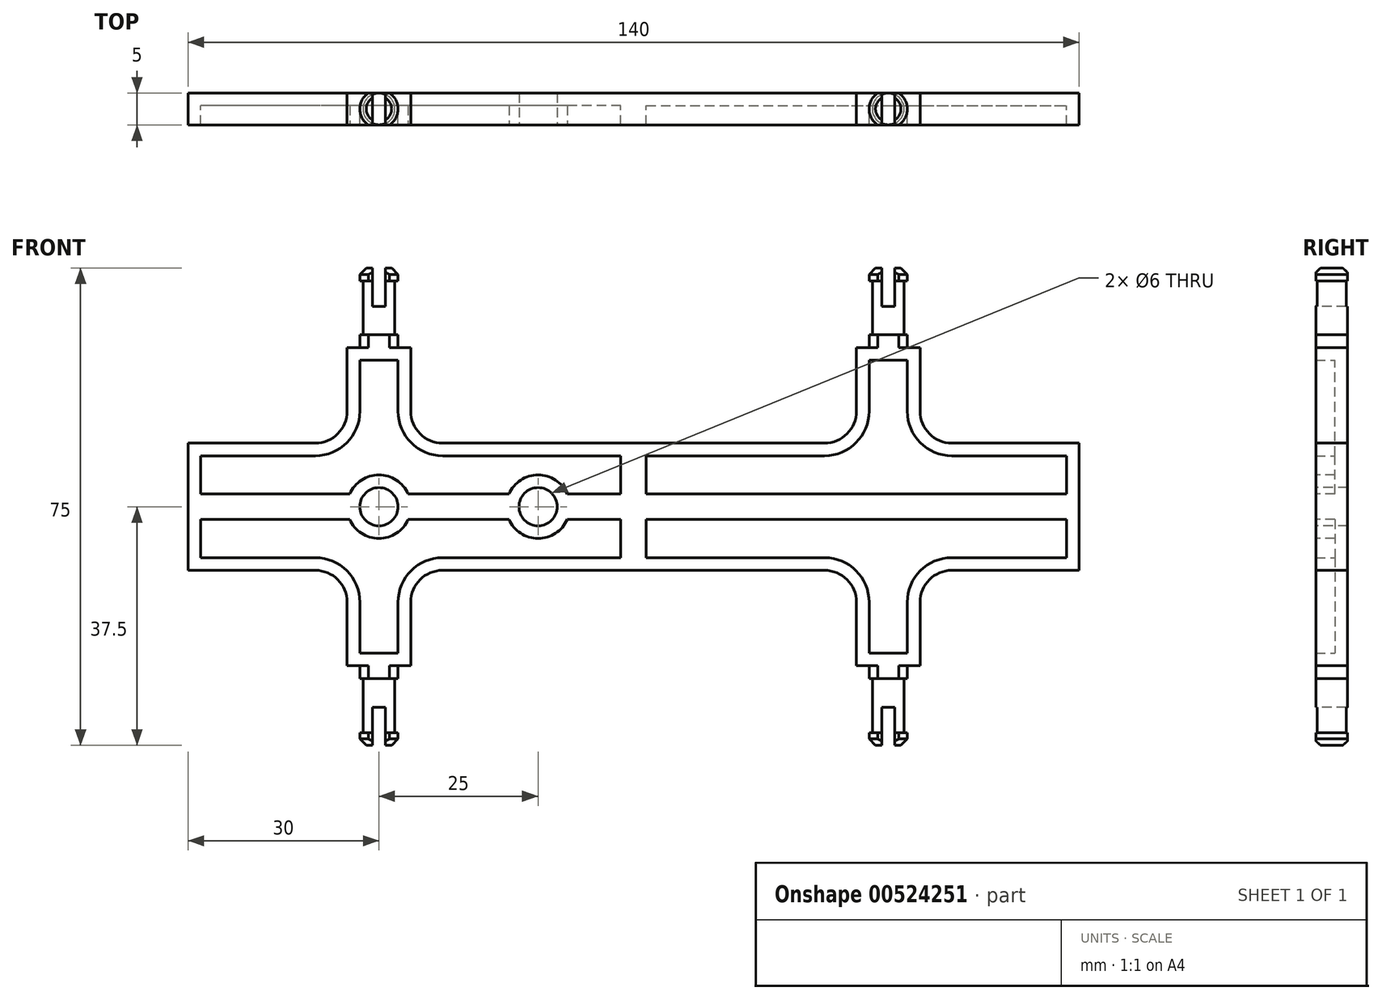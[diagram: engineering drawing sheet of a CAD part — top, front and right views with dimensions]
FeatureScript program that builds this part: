
annotation { "Feature Type Name" : "Feature", "Feature Type Description" : "" }
export const myFeature = defineFeature(function(context is Context, id is Id, definition is map)
    precondition{}
    {
        {
            var Q0;
            Q0=qCreatedBy(makeId("Front.planeOp"),FACE);
            var sketch = newSketch(context, id + "F0", { "sketchPlane" : qUnion([Q0])});
            skLineSegment(sketch, "E0.bottom", {"start": v(0, 0) * mm, "end": v(70, 0) * mm});
            skLineSegment(sketch, "E0.top", {"start": v(0, 10) * mm, "end": v(30, 10) * mm});
            skLineSegment(sketch, "E0.left", {"start": v(0, 0) * mm, "end": v(0, 10) * mm});
            skLineSegment(sketch, "E0.right", {"start": v(70, 0) * mm, "end": v(70, 10) * mm});
            skLineSegment(sketch, "E1.top", {"start": v(35, 25) * mm, "end": v(45, 25) * mm});
            skLineSegment(sketch, "E1.left", {"start": v(35, 15) * mm, "end": v(35, 25) * mm});
            skLineSegment(sketch, "E1.right", {"start": v(45, 15) * mm, "end": v(45, 25) * mm});
            skLineSegment(sketch, "E2.trimOffspring", {"start": v(50, 10) * mm, "end": v(70, 10) * mm});
            skPoint(sketch, "E3.visualSharp", {"position": v(35, 10) * mm});
            skArc(sketch, "E3.filletArc", {"start": v(30, 10) * mm, "mid": v(33.54, 11.46) * mm, "end": v(35, 15) * mm});
            skPoint(sketch, "E4.visualSharp", {"position": v(45, 10) * mm});
            skArc(sketch, "E4.filletArc", {"start": v(45, 15) * mm, "mid": v(46.46, 11.46) * mm, "end": v(50, 10) * mm});
            skSolve(sketch);
        }
        {
            var Q0;
            Q0 = qSketchRegion(id + "F0", true);
            extrude(context, id + "F1", {"entities" : qUnion([Q0]), "endBound" : BoundingType.SYMMETRIC, "depth" : 5 * mm, "offsetDistance" : 25 * mm});
        }
        {
            var Q0;
            Q0=makeQuery(id+"F1.opExtrude","CAP_FACE",FACE,{"disambiguationData":[OSD([sQuery(id+"F0.wireOp",EDGE,"E0.bottom"),sQuery(id+"F0.wireOp",EDGE,"E0.top"),sQuery(id+"F0.wireOp",EDGE,"E0.left"),sQuery(id+"F0.wireOp",EDGE,"E0.right"),sQuery(id+"F0.wireOp",EDGE,"E1.top"),sQuery(id+"F0.wireOp",EDGE,"E1.left"),sQuery(id+"F0.wireOp",EDGE,"E1.right"),sQuery(id+"F0.wireOp",EDGE,"E2.trimOffspring"),sQuery(id+"F0.wireOp",EDGE,"E3.filletArc"),sQuery(id+"F0.wireOp",EDGE,"E4.filletArc")])],"isStart":false});
            shell(context, id + "F2", {"entities" : qUnion([Q0]), "thickness" : 2 * mm});
        }
        {
            var Q0;
            Q0=qCreatedBy(makeId("Front.planeOp"),FACE);
            var sketch = newSketch(context, id + "F3", { "sketchPlane" : qUnion([Q0])});
            skLineSegment(sketch, "E5", {"start": v(40, 25) * mm, "end": v(40, 37.5) * mm});
            skLineSegment(sketch, "E6", {"start": v(40, 37.5) * mm, "end": v(37, 37.5) * mm});
            skLineSegment(sketch, "E7", {"start": v(37, 37.5) * mm, "end": v(37, 35.5) * mm});
            skLineSegment(sketch, "E8", {"start": v(37, 35.5) * mm, "end": v(37.5, 35.5) * mm});
            skLineSegment(sketch, "E9", {"start": v(37.5, 35.5) * mm, "end": v(37.5, 27) * mm});
            skLineSegment(sketch, "E10", {"start": v(37.5, 27) * mm, "end": v(37, 27) * mm});
            skLineSegment(sketch, "E11", {"start": v(37, 27) * mm, "end": v(37, 25) * mm});
            skLineSegment(sketch, "E12", {"start": v(37, 25) * mm, "end": v(40, 25) * mm});
            skSolve(sketch);
        }
        {
            var Q0;
            Q0=makeQuery(id+"F3.imprint","IMPRINT",FACE,{"disambiguationData":[TD([[makeQuery(id+"F3.imprint","IMPRINT",EDGE,{"derivedFrom":sQuery(id+"F3.wireOp",EDGE,"E5")}),1.0]])]});
            var Q1;
            Q1=sQuery(id+"F3.wireOp",EDGE,"E5");
            revolve(context, id + "F4", {"operationType" : NewBodyOperationType.ADD, "entities" : qUnion([Q0]), "axis" : qUnion([Q1]), "revolveType" : RevolveType.FULL});
        }
        {
            var Q0;
            Q0=makeQuery(id+"F4.opRevolve","SWEPT_EDGE",EDGE,{"disambiguationData":[OSD([sQuery(id+"F3.wireOp",EDGE,"E6"),sQuery(id+"F3.wireOp",EDGE,"E7")])]});
            chamfer(context, id + "F5", {"entities" : qUnion([Q0]), "width" : 1 * mm, "tangentPropagation" : true});
        }
        {
            var Q0;
            Q0=makeQuery(id+"F4.opRevolve","SWEPT_FACE",FACE,{"disambiguationData":[OSD([sQuery(id+"F3.wireOp",EDGE,"E6")])]});
            var sketch = newSketch(context, id + "F6", { "sketchPlane" : qUnion([Q0])});
            skLineSegment(sketch, "E13.bottom", {"start": v(-2.5, 2.5) * mm, "end": v(72.5, 2.5) * mm});
            skLineSegment(sketch, "E13.top", {"start": v(-2.5, -2.5) * mm, "end": v(72.5, -2.5) * mm});
            skLineSegment(sketch, "E13.left", {"start": v(-2.5, 2.5) * mm, "end": v(-2.5, -2.5) * mm});
            skLineSegment(sketch, "E13.right", {"start": v(72.5, 2.5) * mm, "end": v(72.5, -2.5) * mm});
            skSolve(sketch);
        }
        {
            var Q0;
            Q0 = qSketchRegion(id + "F6", true);
            extrude(context, id + "F7", {"entities" : qUnion([Q0]), "operationType" : NewBodyOperationType.INTERSECT, "endBound" : BoundingType.THROUGH_ALL, "oppositeDirection" : true, "depth" : 25 * mm, "offsetDistance" : 25 * mm});
        }
        {
            var Q0;
            Q0=makeQuery(id+"F4.opRevolve","SWEPT_FACE",FACE,{"disambiguationData":[OSD([sQuery(id+"F3.wireOp",EDGE,"E6")])]});
            var sketch = newSketch(context, id + "F8", { "sketchPlane" : qUnion([Q0])});
            skLineSegment(sketch, "E14.bottom", {"start": v(39, 4) * mm, "end": v(41, 4) * mm});
            skLineSegment(sketch, "E14.top", {"start": v(39, -4) * mm, "end": v(41, -4) * mm});
            skLineSegment(sketch, "E14.left", {"start": v(39, 4) * mm, "end": v(39, -4) * mm});
            skLineSegment(sketch, "E14.right", {"start": v(41, 4) * mm, "end": v(41, -4) * mm});
            skSolve(sketch);
        }
        {
            var Q0;
            Q0 = qSketchRegion(id + "F8", true);
            extrude(context, id + "F9", {"entities" : qUnion([Q0]), "operationType" : NewBodyOperationType.REMOVE, "oppositeDirection" : true, "depth" : 6 * mm, "offsetDistance" : 25 * mm});
        }
        {
            var Q0;
            Q0=makeQuery(id+"F1.opExtrude","SWEPT_BODY",BODY,{"disambiguationData":[OSD([sQuery(id+"F0.wireOp",EDGE,"E0.bottom"),sQuery(id+"F0.wireOp",EDGE,"E0.top"),sQuery(id+"F0.wireOp",EDGE,"E0.left"),sQuery(id+"F0.wireOp",EDGE,"E0.right"),sQuery(id+"F0.wireOp",EDGE,"E1.top"),sQuery(id+"F0.wireOp",EDGE,"E1.left"),sQuery(id+"F0.wireOp",EDGE,"E1.right"),sQuery(id+"F0.wireOp",EDGE,"E2.trimOffspring"),sQuery(id+"F0.wireOp",EDGE,"E3.filletArc"),sQuery(id+"F0.wireOp",EDGE,"E4.filletArc")])]});
            var Q1;
            Q1=qCreatedBy(makeId("Right.planeOp"),FACE);
            mirror(context, id + "F10", {"operationType" : NewBodyOperationType.ADD, "entities" : qUnion([Q0]), "mirrorPlane" : qUnion([Q1])});
        }
        {
            var Q0;
            Q0=makeQuery(id+"F1.opExtrude","SWEPT_BODY",BODY,{"disambiguationData":[OSD([sQuery(id+"F0.wireOp",EDGE,"E0.bottom"),sQuery(id+"F0.wireOp",EDGE,"E0.top"),sQuery(id+"F0.wireOp",EDGE,"E0.left"),sQuery(id+"F0.wireOp",EDGE,"E0.right"),sQuery(id+"F0.wireOp",EDGE,"E1.top"),sQuery(id+"F0.wireOp",EDGE,"E1.left"),sQuery(id+"F0.wireOp",EDGE,"E1.right"),sQuery(id+"F0.wireOp",EDGE,"E2.trimOffspring"),sQuery(id+"F0.wireOp",EDGE,"E3.filletArc"),sQuery(id+"F0.wireOp",EDGE,"E4.filletArc")])]});
            var Q1;
            Q1=qCreatedBy(makeId("Top.planeOp"),FACE);
            mirror(context, id + "F11", {"operationType" : NewBodyOperationType.ADD, "entities" : qUnion([Q0]), "mirrorPlane" : qUnion([Q1])});
        }
        {
            var Q0;
            {var subQ0=makeQuery(id+"F7.boolean.opBoolean","MERGE",FACE,{"derivedFrom":[makeQuery(id+"F1.opExtrude","CAP_FACE",FACE,{"disambiguationData":[OSD([sQuery(id+"F0.wireOp",EDGE,"E0.bottom"),sQuery(id+"F0.wireOp",EDGE,"E0.top"),sQuery(id+"F0.wireOp",EDGE,"E0.left"),sQuery(id+"F0.wireOp",EDGE,"E0.right"),sQuery(id+"F0.wireOp",EDGE,"E1.top"),sQuery(id+"F0.wireOp",EDGE,"E1.left"),sQuery(id+"F0.wireOp",EDGE,"E1.right"),sQuery(id+"F0.wireOp",EDGE,"E2.trimOffspring"),sQuery(id+"F0.wireOp",EDGE,"E3.filletArc"),sQuery(id+"F0.wireOp",EDGE,"E4.filletArc")])],"isStart":false}),makeQuery(id+"F7.boolean.toolComplement.opBoolean","COPY",FACE,{"derivedFrom":makeQuery(id+"F7.opExtrude","SWEPT_FACE",FACE,{"disambiguationData":[OSD([sQuery(id+"F6.wireOp",EDGE,"E13.top")])]})})]});var subQ1=makeQuery(id+"F10.boolean.opBoolean","MERGE",FACE,{"derivedFrom":[subQ0,makeQuery(id+"F10.opPattern","COPY",FACE,{"derivedFrom":subQ0,"instanceName":"1"})]});Q0=makeQuery(id+"F11.boolean.opBoolean","MERGE",FACE,{"derivedFrom":[subQ1,makeQuery(id+"F11.opPattern","COPY",FACE,{"derivedFrom":subQ1,"instanceName":"1"})]});}
            var sketch = newSketch(context, id + "F12", { "sketchPlane" : qUnion([Q0])});
            skCircle(sketch, "E15", {"center": v(-40, 0) * mm, "radius": 5 * mm});
            skCircle(sketch, "E16", {"center": v(-15, 0) * mm, "radius": 5 * mm});
            skSolve(sketch);
        }
        {
            var Q0;
            Q0 = qSketchRegion(id + "F12", true);
            extrude(context, id + "F13", {"entities" : qUnion([Q0]), "operationType" : NewBodyOperationType.ADD, "endBound" : BoundingType.UP_TO_NEXT, "oppositeDirection" : true, "depth" : 25 * mm, "offsetDistance" : 25 * mm});
        }
        {
            var Q0;
            {var subQ0=makeQuery(id+"F7.boolean.opBoolean","MERGE",FACE,{"derivedFrom":[makeQuery(id+"F1.opExtrude","CAP_FACE",FACE,{"disambiguationData":[OSD([sQuery(id+"F0.wireOp",EDGE,"E0.bottom"),sQuery(id+"F0.wireOp",EDGE,"E0.top"),sQuery(id+"F0.wireOp",EDGE,"E0.left"),sQuery(id+"F0.wireOp",EDGE,"E0.right"),sQuery(id+"F0.wireOp",EDGE,"E1.top"),sQuery(id+"F0.wireOp",EDGE,"E1.left"),sQuery(id+"F0.wireOp",EDGE,"E1.right"),sQuery(id+"F0.wireOp",EDGE,"E2.trimOffspring"),sQuery(id+"F0.wireOp",EDGE,"E3.filletArc"),sQuery(id+"F0.wireOp",EDGE,"E4.filletArc")])],"isStart":false}),makeQuery(id+"F7.boolean.toolComplement.opBoolean","COPY",FACE,{"derivedFrom":makeQuery(id+"F7.opExtrude","SWEPT_FACE",FACE,{"disambiguationData":[OSD([sQuery(id+"F6.wireOp",EDGE,"E13.top")])]})})]});var subQ1=makeQuery(id+"F10.boolean.opBoolean","MERGE",FACE,{"derivedFrom":[subQ0,makeQuery(id+"F10.opPattern","COPY",FACE,{"derivedFrom":subQ0,"instanceName":"1"})]});Q0=makeQuery(id+"F13.boolean.opBoolean","MERGE",FACE,{"derivedFrom":[makeQuery(id+"F11.boolean.opBoolean","MERGE",FACE,{"derivedFrom":[subQ1,makeQuery(id+"F11.opPattern","COPY",FACE,{"derivedFrom":subQ1,"instanceName":"1"})]}),makeQuery(id+"F13.opExtrude","CAP_FACE",FACE,{"disambiguationData":[OSD([sQuery(id+"F12.wireOp",EDGE,"E15")])],"isStart":true}),makeQuery(id+"F13.opExtrude","CAP_FACE",FACE,{"disambiguationData":[OSD([sQuery(id+"F12.wireOp",EDGE,"E16")])],"isStart":true})]});}
            var sketch = newSketch(context, id + "F14", { "sketchPlane" : qUnion([Q0])});
            skPoint(sketch, "E17", {"position": v(-40, 0) * mm});
            skPoint(sketch, "E18", {"position": v(-15, 0) * mm});
            skSolve(sketch);
        }
        {
            var Q0;
            Q0=sQuery(id+"F14.wireOp",VERTEX,"E17");
            var Q1;
            Q1=sQuery(id+"F14.wireOp",VERTEX,"E18");
            var Q2;
            Q2=makeQuery(id+"F1.opExtrude","SWEPT_BODY",BODY,{"disambiguationData":[OSD([sQuery(id+"F0.wireOp",EDGE,"E0.bottom"),sQuery(id+"F0.wireOp",EDGE,"E0.top"),sQuery(id+"F0.wireOp",EDGE,"E0.left"),sQuery(id+"F0.wireOp",EDGE,"E0.right"),sQuery(id+"F0.wireOp",EDGE,"E1.top"),sQuery(id+"F0.wireOp",EDGE,"E1.left"),sQuery(id+"F0.wireOp",EDGE,"E1.right"),sQuery(id+"F0.wireOp",EDGE,"E2.trimOffspring"),sQuery(id+"F0.wireOp",EDGE,"E3.filletArc"),sQuery(id+"F0.wireOp",EDGE,"E4.filletArc")])]});
            hole(context, id + "F15", {"style" : HoleStyle.SIMPLE, "endStyle" : HoleEndStyle.THROUGH, "holeDiameter" : 6 * mm, "majorDiameter" : 5 * mm, "isTappedThrough" : true, "tappedDepth" : 12 * mm, "tapClearance" : 3, "locations" : qUnion([Q0, Q1]), "scope" : qUnion([Q2])});
        }
    });
